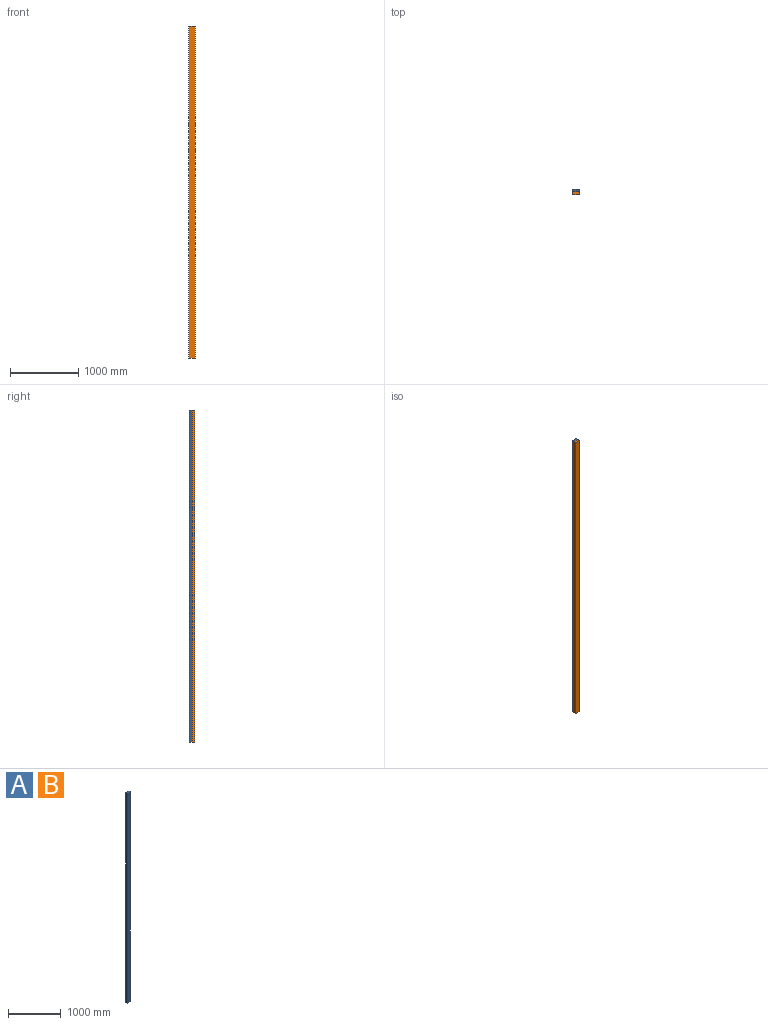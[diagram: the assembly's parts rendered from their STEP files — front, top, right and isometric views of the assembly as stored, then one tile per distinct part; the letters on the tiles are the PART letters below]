
ASSEMBLY  parts=2 mates=1
PART A: 6 faces, bbox 88.9x38.1x4876.8 mm
  f0: plane 4876.8x88.9mm, normal (0,-1,0), area 433547.5mm2, adj f1,f3,f4,f5
  f1: plane 4876.8x38.1mm, normal (1,0,0), area 185806.1mm2, adj f0,f2,f4,f5
  f2: plane 4876.8x88.9mm, normal (0,1,0), area 433547.5mm2, adj f1,f3,f4,f5
  f3: plane 4876.8x38.1mm, normal (-1,0,0), area 185806.1mm2, adj f0,f2,f4,f5
  f4: plane 88.9x38.1mm, normal (0,0,1), area 3387.1mm2, adj f0,f1,f2,f3
  f5: plane 88.9x38.1mm, normal (0,0,-1), area 3387.1mm2, adj f0,f1,f2,f3
PART B: same geometry as A
PLACE A t=(-0.29,37.59,0)mm
PLACE B t=(-0.29,-0.51,0)mm fixed
MATE fastened A.f0 <-> B.f2  axis (0,-1,0) through (-0.29,18.54,0)mm
